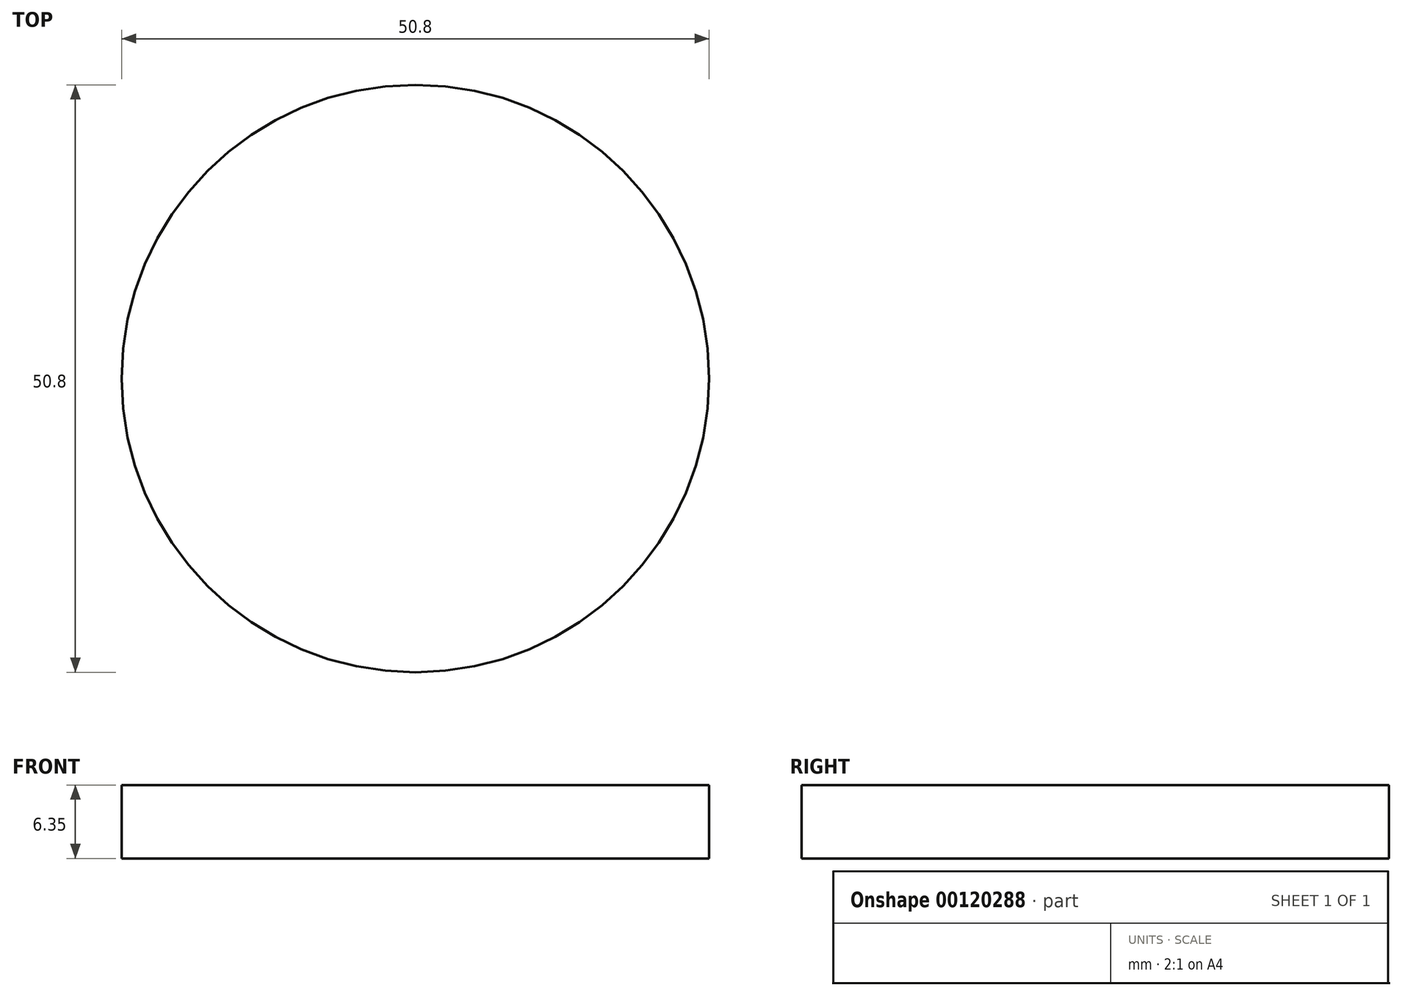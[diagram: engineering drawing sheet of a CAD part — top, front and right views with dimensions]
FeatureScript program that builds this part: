
annotation { "Feature Type Name" : "Feature", "Feature Type Description" : "" }
export const myFeature = defineFeature(function(context is Context, id is Id, definition is map)
    precondition{}
    {
        {
            var Q0;
            Q0=qCreatedBy(makeId("Top.planeOp"),FACE);
            var sketch = newSketch(context, id + "F0", { "sketchPlane" : qUnion([Q0])});
            skCircle(sketch, "E0", {"center": v(0, 0) * mm, "radius": 25.4 * mm});
            skSolve(sketch);
        }
        {
            var Q0;
            Q0 = qSketchRegion(id + "F0", true);
            extrude(context, id + "F1", {"entities" : qUnion([Q0]), "depth" : 6.35 * mm});
        }
    });
